# Revit family: CFP
name_source: partatom
category: Lighting Fixtures
units: mm (PartAtom-declared; Revit-internal decimal feet)

## family parameters
Cut with Voids When Loaded = No
Host = Face
Light Source = Yes
OmniClass Number = 23.80.70.11
OmniClass Title = Luminaries for Internal Lighting
Part Type = Normal
Room Calculation Point = No
Round Connector Dimension = Use Diameter
Shared = No

## types (4) — shared parameters
Assembly Code = D5020200
Color Filter = 16777215
Default Elevation = 4' - 0"
Description = Edge-lit Flat Panel
Dimming Lamp Color Temperature Shift = <None>
Emit Shape Visible in Rendering = No
Emit from Rectangle Width = 1' - 9 7/8"
Lamp = LED Lamp
Load Classification = Lighting
Manufacturer = Columbia Lighting
Material Finish = Paint  - White
Model = CFP
Mounting Type = Recessed mount
Opal lens = White Glass
Power Factor = 1
Tilt Angle = -90.00°
URL = https://www.currentlighting.com
Voltage = 120 V
Warranty = Five year warranty
Wattage Comments = 31.7W to 40.1W
zz Length 2 = 1' - 11 7/8"

## per-type parameters (varying)
| type | Apparent Load | Emit from Rectangle Length | Photometric Web File | Watts | zz Length 1 |
| CFP24-4135 | 40 VA | 3' - 9 7/8" | CFP24-4135.ies | 40 W | 3' - 11 7/8" |
| CFP24-4140 | 40 VA | 3' - 9 7/8" | CFP24-4140.ies | 40 W | 3' - 11 7/8" |
| CFP22-3335 | 32 VA | 1' - 9 7/8" | CFP22-3335.ies | 32 W | 1' - 11 7/8" |
| CFP22-3340 | 32 VA | 1' - 9 7/8" | CFP22-3340.ies | 32 W | 1' - 11 7/8" |

## geometry (parser evidence)
native form markers: Sweep x2
no freeform markers — native parametric forms only
